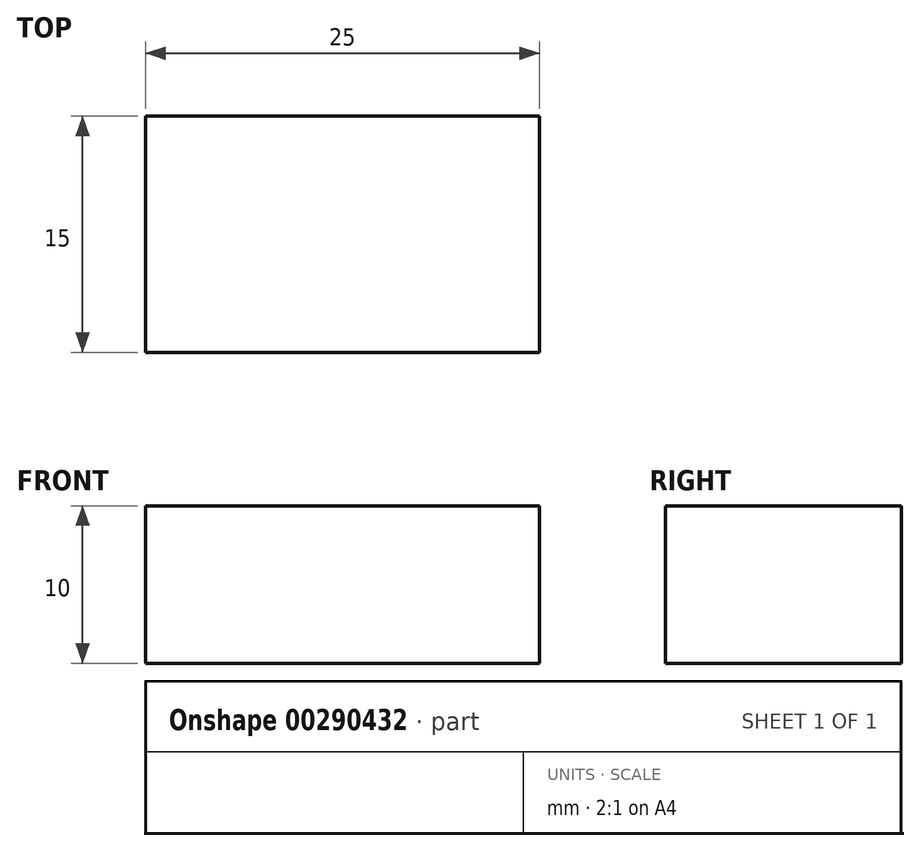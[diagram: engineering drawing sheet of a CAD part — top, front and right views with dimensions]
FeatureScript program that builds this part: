
annotation { "Feature Type Name" : "Feature", "Feature Type Description" : "" }
export const myFeature = defineFeature(function(context is Context, id is Id, definition is map)
    precondition{}
    {
        {
            var Q0;
            Q0=qCreatedBy(makeId("Front.planeOp"),FACE);
            var sketch = newSketch(context, id + "F0", { "sketchPlane" : qUnion([Q0])});
            skLineSegment(sketch, "E0", {"start": v(-12.5, 10) * mm, "end": v(-12.5, 0) * mm});
            skLineSegment(sketch, "E1", {"start": v(-12.5, 0) * mm, "end": v(12.5, 0) * mm});
            skLineSegment(sketch, "E2", {"start": v(12.5, 0) * mm, "end": v(12.5, 10) * mm});
            skLineSegment(sketch, "E3", {"start": v(12.5, 10) * mm, "end": v(-12.5, 10) * mm});
            skSolve(sketch);
        }
        {
            var Q0;
            Q0 = qSketchRegion(id + "F0", true);
            extrude(context, id + "F1", {"entities" : qUnion([Q0]), "endBound" : BoundingType.SYMMETRIC, "depth" : 15 * mm});
        }
    });
